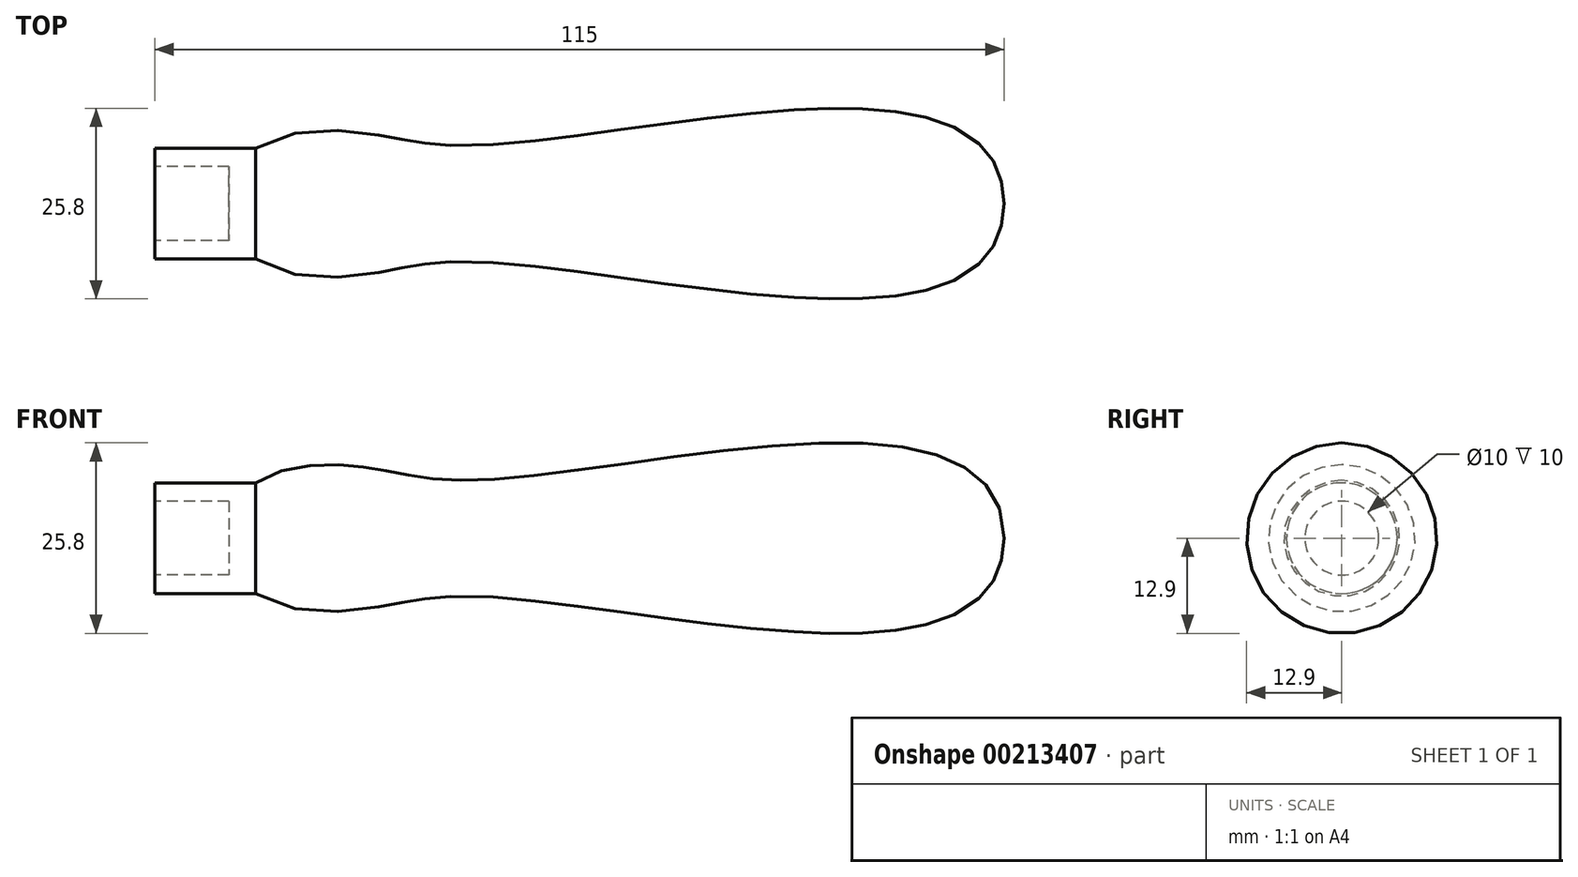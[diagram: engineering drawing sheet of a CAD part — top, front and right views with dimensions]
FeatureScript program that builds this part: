
annotation { "Feature Type Name" : "Feature", "Feature Type Description" : "" }
export const myFeature = defineFeature(function(context is Context, id is Id, definition is map)
    precondition{}
    {
        {
            var Q0;
            Q0=qCreatedBy(makeId("Front.planeOp"),FACE);
            var sketch = newSketch(context, id + "F0", { "sketchPlane" : qUnion([Q0])});
            skLineSegment(sketch, "E0", {"start": v(0, 0) * mm, "end": v(105, 0) * mm});
            skFitSpline(sketch, "E1", {"points": [v(0, 0) * mm, v(15.3, 9.9) * mm, v(32.13, 7.84) * mm, v(87.66, 12.74) * mm, v(105, 0) * mm], "startDerivative": vector(0, 129.61) * mm, "endDerivative": vector(0, -112) * mm});
            skLineSegment(sketch, "E2", {"start": v(105, 0) * mm, "end": v(105, 16.9) * mm, "construction": true});
            skLineSegment(sketch, "E3", {"start": v(0, 0) * mm, "end": v(-18.64, 0) * mm, "construction": true});
            skSolve(sketch);
        }
        {
            var Q0;
            Q0=makeQuery(id+"F0.imprint","IMPRINT",FACE,{"disambiguationData":[TD([[makeQuery(id+"F0.imprint","IMPRINT",EDGE,{"derivedFrom":sQuery(id+"F0.wireOp",EDGE,"E0")}),1.0]])]});
            var Q1;
            Q1=sQuery(id+"F0.wireOp",EDGE,"E3");
            revolve(context, id + "F1", {"entities" : qUnion([Q0]), "axis" : qUnion([Q1]), "revolveType" : RevolveType.FULL});
        }
        {
            var Q0;
            Q0=qCreatedBy(makeId("Right.planeOp"),FACE);
            var sketch = newSketch(context, id + "F2", { "sketchPlane" : qUnion([Q0])});
            skCircle(sketch, "E4", {"center": v(0, 0) * mm, "radius": 7.5 * mm});
            skSolve(sketch);
        }
        {
            var Q0;
            Q0 = qSketchRegion(id + "F2", true);
            extrude(context, id + "F3", {"entities" : qUnion([Q0]), "operationType" : NewBodyOperationType.ADD, "endBound" : BoundingType.UP_TO_NEXT, "depth" : 25 * mm, "hasSecondDirection" : true, "secondDirectionOppositeDirection" : true, "secondDirectionDepth" : 10 * mm});
        }
        {
            var Q0;
            Q0=makeQuery(id+"F3.opExtrude","CAP_FACE",FACE,{"disambiguationData":[OSD([sQuery(id+"F2.wireOp",EDGE,"E4")])],"isStart":true});
            var sketch = newSketch(context, id + "F4", { "sketchPlane" : qUnion([Q0])});
            skCircle(sketch, "E5", {"center": v(0, 0) * mm, "radius": 5 * mm});
            skSolve(sketch);
        }
        {
            var Q0;
            Q0 = qSketchRegion(id + "F4", true);
            extrude(context, id + "F5", {"entities" : qUnion([Q0]), "operationType" : NewBodyOperationType.REMOVE, "oppositeDirection" : true, "depth" : 10 * mm});
        }
    });
